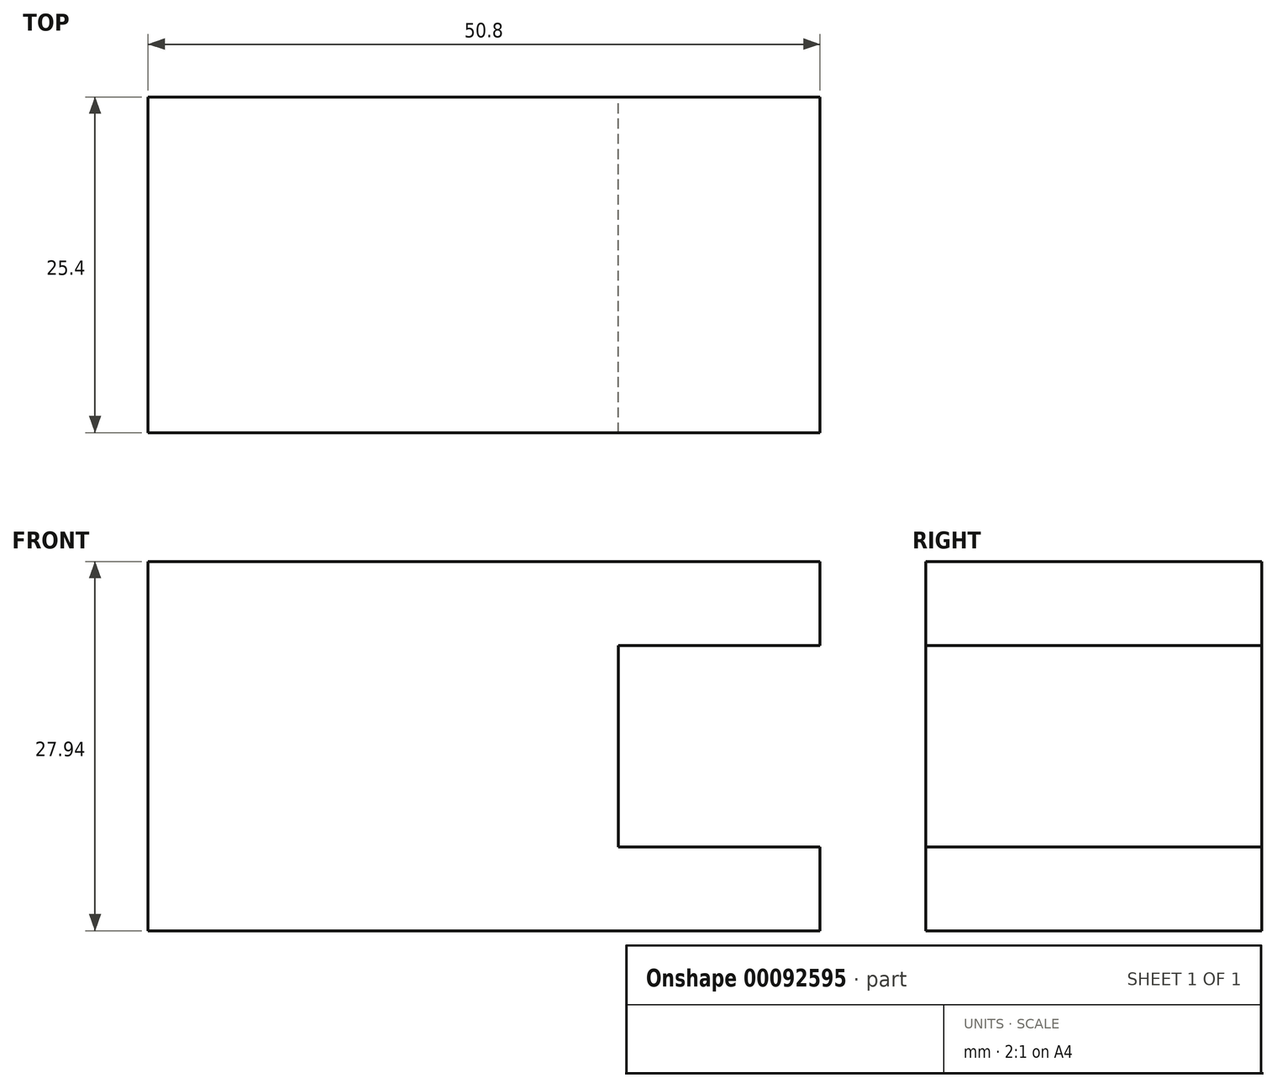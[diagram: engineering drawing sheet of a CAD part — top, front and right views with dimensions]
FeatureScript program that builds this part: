
annotation { "Feature Type Name" : "Feature", "Feature Type Description" : "" }
export const myFeature = defineFeature(function(context is Context, id is Id, definition is map)
    precondition{}
    {
        {
            var Q0;
            Q0=qCreatedBy(makeId("Front.planeOp"),FACE);
            var sketch = newSketch(context, id + "F0", { "sketchPlane" : qUnion([Q0])});
            skLineSegment(sketch, "E0", {"start": v(0, 0) * mm, "end": v(0, 27.94) * mm});
            skLineSegment(sketch, "E1", {"start": v(0, 27.94) * mm, "end": v(50.8, 27.94) * mm});
            skLineSegment(sketch, "E2", {"start": v(50.8, 27.94) * mm, "end": v(50.8, 21.59) * mm});
            skLineSegment(sketch, "E3", {"start": v(50.8, 21.59) * mm, "end": v(35.56, 21.59) * mm});
            skLineSegment(sketch, "E4", {"start": v(35.56, 21.59) * mm, "end": v(35.56, 6.35) * mm});
            skLineSegment(sketch, "E5", {"start": v(35.56, 6.35) * mm, "end": v(50.8, 6.35) * mm});
            skLineSegment(sketch, "E6", {"start": v(50.8, 6.35) * mm, "end": v(50.8, 0) * mm});
            skLineSegment(sketch, "E7", {"start": v(50.8, 0) * mm, "end": v(0, 0) * mm});
            skSolve(sketch);
        }
        {
            var Q0;
            Q0 = qSketchRegion(id + "F0", true);
            extrude(context, id + "F1", {"entities" : qUnion([Q0]), "depth" : 25.4 * mm});
        }
    });
